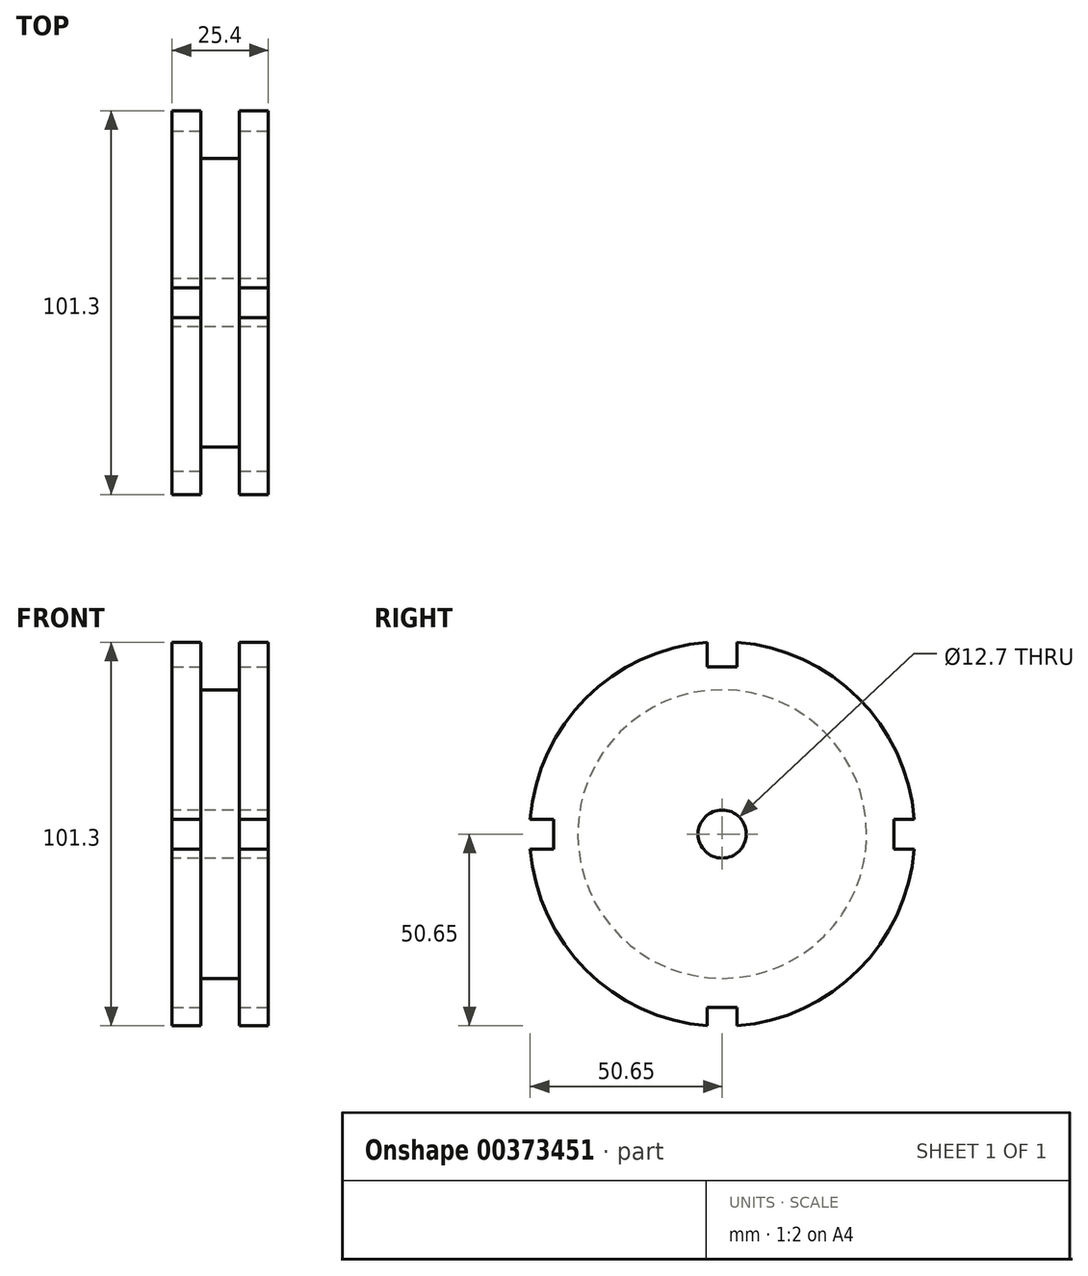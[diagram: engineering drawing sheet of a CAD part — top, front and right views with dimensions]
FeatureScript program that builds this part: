
annotation { "Feature Type Name" : "Feature", "Feature Type Description" : "" }
export const myFeature = defineFeature(function(context is Context, id is Id, definition is map)
    precondition{}
    {
        {
            var Q0;
            Q0=qCreatedBy(makeId("Front.planeOp"),FACE);
            var sketch = newSketch(context, id + "F0", { "sketchPlane" : qUnion([Q0])});
            skLineSegment(sketch, "E0", {"start": v(-19.78, 0) * mm, "end": v(33.7, 0) * mm});
            skLineSegment(sketch, "E1", {"start": v(12.7, 6.35) * mm, "end": v(12.7, 50.8) * mm});
            skLineSegment(sketch, "E2", {"start": v(12.7, 50.8) * mm, "end": v(5.08, 50.8) * mm});
            skLineSegment(sketch, "E3", {"start": v(5.08, 50.8) * mm, "end": v(5.08, 38.1) * mm});
            skLineSegment(sketch, "E4", {"start": v(5.08, 38.1) * mm, "end": v(-5.08, 38.1) * mm});
            skLineSegment(sketch, "E5", {"start": v(12.7, 6.35) * mm, "end": v(-12.7, 6.35) * mm});
            skLineSegment(sketch, "E6", {"start": v(-12.7, 6.35) * mm, "end": v(-12.7, 50.8) * mm});
            skLineSegment(sketch, "E7", {"start": v(-12.7, 50.8) * mm, "end": v(-5.08, 50.8) * mm});
            skLineSegment(sketch, "E8", {"start": v(-5.08, 50.8) * mm, "end": v(-5.08, 38.1) * mm});
            skSolve(sketch);
        }
        {
            var Q0;
            Q0 = qSketchRegion(id + "F0", true);
            var Q1;
            Q1=sQuery(id+"F0.wireOp",EDGE,"E0");
            revolve(context, id + "F1", {"entities" : qUnion([Q0]), "axis" : qUnion([Q1]), "revolveType" : RevolveType.FULL});
        }
        {
            var Q0;
            Q0=makeQuery(id+"F1.opRevolve","SWEPT_FACE",FACE,{"disambiguationData":[OSD([sQuery(id+"F0.wireOp",EDGE,"E1")])]});
            var sketch = newSketch(context, id + "F2", { "sketchPlane" : qUnion([Q0])});
            skLineSegment(sketch, "E9.bottom", {"start": v(3.94, 44.13) * mm, "end": v(-3.94, 44.13) * mm});
            skLineSegment(sketch, "E9.top", {"start": v(3.94, 57.47) * mm, "end": v(-3.94, 57.47) * mm});
            skLineSegment(sketch, "E9.left", {"start": v(3.94, 44.13) * mm, "end": v(3.94, 57.47) * mm});
            skLineSegment(sketch, "E9.right", {"start": v(-3.94, 44.13) * mm, "end": v(-3.94, 57.47) * mm});
            skPoint(sketch, "E9.middle", {"position": v(0, 50.8) * mm});
            skLineSegment(sketch, "E10.bottom", {"start": v(45.31, 3.94) * mm, "end": v(56.29, 3.94) * mm});
            skLineSegment(sketch, "E10.top", {"start": v(45.31, -3.94) * mm, "end": v(56.29, -3.94) * mm});
            skLineSegment(sketch, "E10.left", {"start": v(45.31, 3.94) * mm, "end": v(45.31, -3.94) * mm});
            skLineSegment(sketch, "E10.right", {"start": v(56.29, 3.94) * mm, "end": v(56.29, -3.94) * mm});
            skPoint(sketch, "E10.middle", {"position": v(50.8, 0) * mm});
            skLineSegment(sketch, "E11.bottom", {"start": v(3.94, -45.71) * mm, "end": v(-3.94, -45.71) * mm});
            skLineSegment(sketch, "E11.top", {"start": v(3.94, -55.89) * mm, "end": v(-3.94, -55.89) * mm});
            skLineSegment(sketch, "E11.left", {"start": v(3.94, -45.71) * mm, "end": v(3.94, -55.89) * mm});
            skLineSegment(sketch, "E11.right", {"start": v(-3.94, -45.71) * mm, "end": v(-3.94, -55.89) * mm});
            skPoint(sketch, "E11.middle", {"position": v(0, -50.8) * mm});
            skLineSegment(sketch, "E12.bottom", {"start": v(-44.53, -3.94) * mm, "end": v(-57.07, -3.94) * mm});
            skLineSegment(sketch, "E12.top", {"start": v(-44.53, 3.94) * mm, "end": v(-57.07, 3.94) * mm});
            skLineSegment(sketch, "E12.left", {"start": v(-44.53, -3.94) * mm, "end": v(-44.53, 3.94) * mm});
            skLineSegment(sketch, "E12.right", {"start": v(-57.07, -3.94) * mm, "end": v(-57.07, 3.94) * mm});
            skPoint(sketch, "E12.middle", {"position": v(-50.8, 0) * mm});
            skSolve(sketch);
        }
        {
            var Q0;
            Q0 = qSketchRegion(id + "F2", true);
            extrude(context, id + "F3", {"entities" : qUnion([Q0]), "operationType" : NewBodyOperationType.REMOVE, "endBound" : BoundingType.THROUGH_ALL, "oppositeDirection" : true, "depth" : 25.4 * mm});
        }
    });
